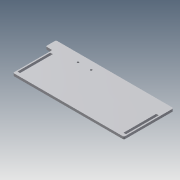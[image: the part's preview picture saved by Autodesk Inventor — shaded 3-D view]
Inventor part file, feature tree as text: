
AUTODESK INVENTOR PART (.ipt)
format: ipt  version: 2014 (Build 180170000, 170)  size: 128,512 bytes
history: native  units: mm
features: extrude x4, sketch x4, fillet x2
ambient origin geometry x8: Origin, YZ Plane, XZ Plane, XY Plane, X Axis, Y Axis, Z Axis, Center Point
bodies: Solid1 (feature_tree)
feature tree (10):
  extrude  "Extrusion1"  Depth=268.0mm
  extrude  "Extrusion2"  Depth=6.25mm
  fillet  "Fillet2"  Radius=2.875mm
  extrude  "Extrusion3"  Depth=3.0mm
  fillet  "Fillet3"  Radius=25.0mm
  extrude  "Extrusion5"  Depth=3.0mm
  sketch  "Sketch1"  dims[d0=95.0mm d1=268.0mm]
  sketch  "Sketch2"  dims[d2=6.0mm d3=0.0mm d4=6.25mm d5=2.875mm]
  sketch  "Sketch3"  dims[d8=10.0mm d9=0.0mm d11=3.0mm d12=25.0mm]
  sketch  "Sketch5"  dims[d15=6.0mm d16=0.0mm d17=3.0mm d23=8.0mm d24=2.875mm d25=150.0mm d26=72.694mm d27=31.75mm d28=19.447mm d29=4.572mm d30=10.0mm d31=0.0mm]
